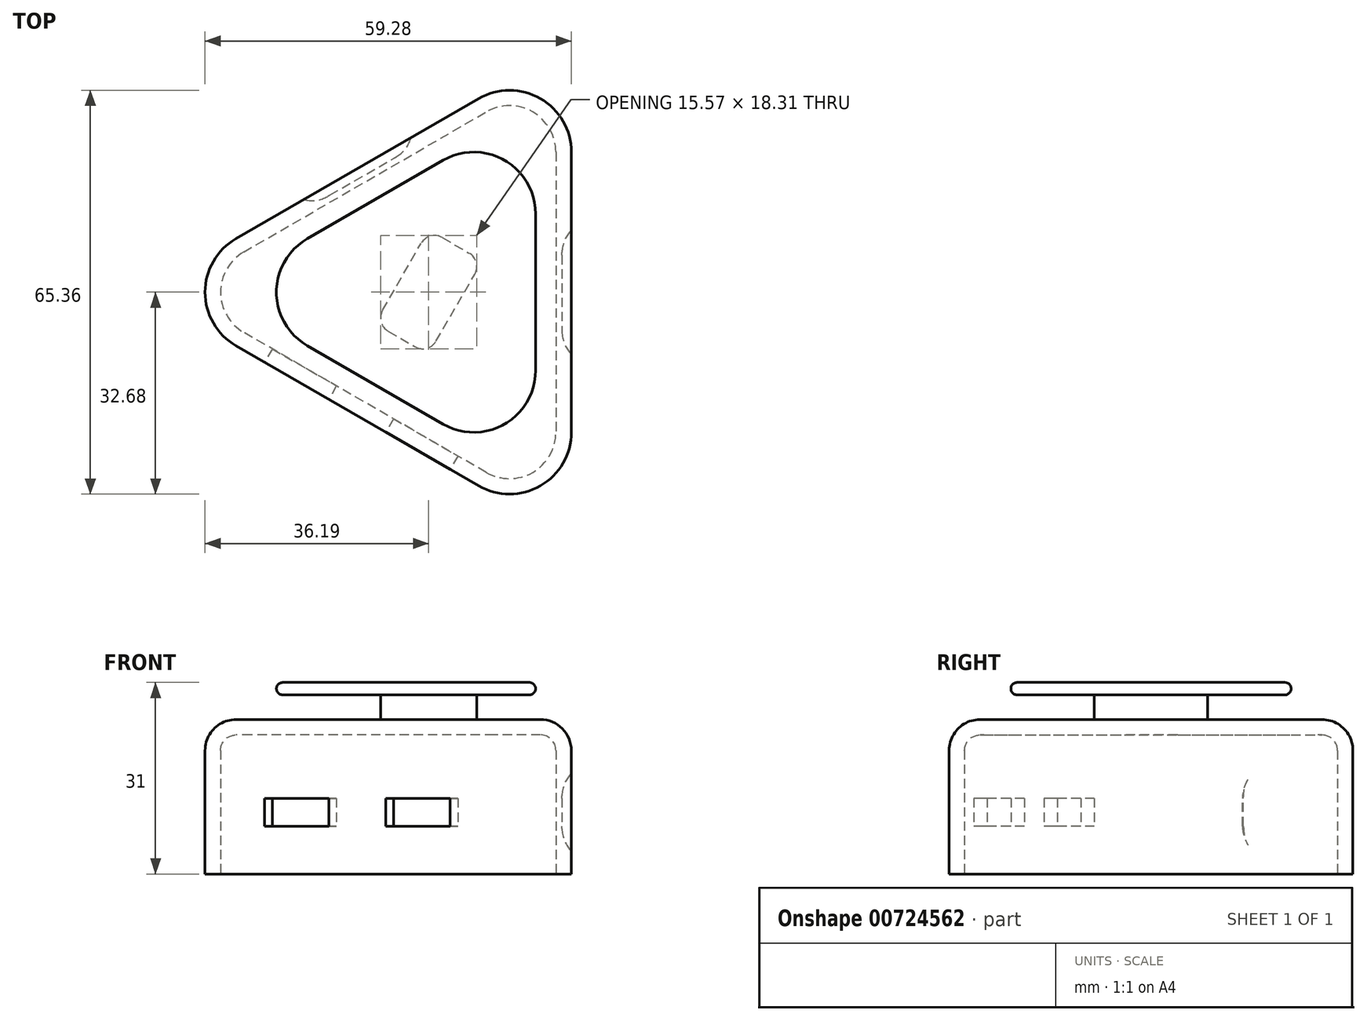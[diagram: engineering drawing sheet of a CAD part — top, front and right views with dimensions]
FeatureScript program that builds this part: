
annotation { "Feature Type Name" : "Feature", "Feature Type Description" : "" }
export const myFeature = defineFeature(function(context is Context, id is Id, definition is map)
    precondition{}
    {
        {
            var Q0;
            Q0=qCreatedBy(makeId("Top.planeOp"),FACE);
            var sketch = newSketch(context, id + "F0", { "sketchPlane" : qUnion([Q0])});
            skCircle(sketch, "E0.cCircle", {"center": v(0, 0) * mm, "radius": 23.1 * mm, "construction": true});
            skLineSegment(sketch, "E0.0", {"start": v(23.1, 40) * mm, "end": v(23.1, -40) * mm});
            skLineSegment(sketch, "E0.1", {"start": v(23.1, -40) * mm, "end": v(-46.19, 0) * mm});
            skLineSegment(sketch, "E0.2", {"start": v(-46.19, 0) * mm, "end": v(23.1, 40) * mm});
            skPoint(sketch, "E0.0.midPoint", {"position": v(23.1, 0) * mm});
            skSolve(sketch);
        }
        {
            var Q0;
            Q0=makeQuery(id+"F0.imprint","IMPRINT",FACE,{"disambiguationData":[TD([[makeQuery(id+"F0.imprint","IMPRINT",EDGE,{"derivedFrom":sQuery(id+"F0.wireOp",EDGE,"E0.0")}),-1.0]])]});
            extrude(context, id + "F1", {"entities" : qUnion([Q0]), "depth" : 25 * mm, "offsetDistance" : 25 * mm});
        }
        {
            var Q0;
            Q0=makeQuery(id+"F1.opExtrude","SWEPT_EDGE",EDGE,{"disambiguationData":[OSD([sQuery(id+"F0.wireOp",EDGE,"E0.1"),sQuery(id+"F0.wireOp",EDGE,"E0.2")])]});
            var Q1;
            Q1=makeQuery(id+"F1.opExtrude","SWEPT_EDGE",EDGE,{"disambiguationData":[OSD([sQuery(id+"F0.wireOp",EDGE,"E0.0"),sQuery(id+"F0.wireOp",EDGE,"E0.1")])]});
            var Q2;
            Q2=makeQuery(id+"F1.opExtrude","SWEPT_EDGE",EDGE,{"disambiguationData":[OSD([sQuery(id+"F0.wireOp",EDGE,"E0.0"),sQuery(id+"F0.wireOp",EDGE,"E0.2")])]});
            fillet(context, id + "F2", {"entities" : qUnion([Q0, Q1, Q2]), "radius" : 10 * mm, "tangentPropagation" : true, "allowEdgeOverflow" : false});
        }
        {
            var Q0;
            Q0=makeQuery(id+"F1.opExtrude","CAP_EDGE",EDGE,{"disambiguationData":[OSD([sQuery(id+"F0.wireOp",EDGE,"E0.1")])],"isStart":false});
            fillet(context, id + "F3", {"entities" : qUnion([Q0]), "radius" : 5 * mm, "tangentPropagation" : true, "allowEdgeOverflow" : false});
        }
        {
            var Q0;
            Q0=makeQuery(id+"F1.opExtrude","CAP_FACE",FACE,{"disambiguationData":[OSD([sQuery(id+"F0.wireOp",EDGE,"E0.0"),sQuery(id+"F0.wireOp",EDGE,"E0.1"),sQuery(id+"F0.wireOp",EDGE,"E0.2")])],"isStart":true});
            shell(context, id + "F4", {"entities" : qUnion([Q0]), "thickness" : 2.5 * mm});
        }
        {
            var Q0;
            Q0=makeQuery(id+"F1.opExtrude","CAP_FACE",FACE,{"disambiguationData":[OSD([sQuery(id+"F0.wireOp",EDGE,"E0.0"),sQuery(id+"F0.wireOp",EDGE,"E0.1"),sQuery(id+"F0.wireOp",EDGE,"E0.2")])],"isStart":false});
            var sketch = newSketch(context, id + "F5", { "sketchPlane" : qUnion([Q0])});
            skLineSegment(sketch, "E1.bottom", {"start": v(-8.7, -5.08) * mm, "end": v(0.04, 10.08) * mm});
            skLineSegment(sketch, "E1.top", {"start": v(-0.04, -10.08) * mm, "end": v(8.7, 5.08) * mm});
            skLineSegment(sketch, "E1.left", {"start": v(-8.7, -5.08) * mm, "end": v(-0.04, -10.08) * mm});
            skLineSegment(sketch, "E1.right", {"start": v(0.04, 10.08) * mm, "end": v(8.7, 5.08) * mm});
            skPoint(sketch, "E1.middle", {"position": v(0, 0) * mm});
            skSolve(sketch);
        }
        {
            var Q0;
            Q0=makeQuery(id+"F5.imprint","IMPRINT",FACE,{"disambiguationData":[TD([[makeQuery(id+"F5.imprint","IMPRINT",EDGE,{"derivedFrom":sQuery(id+"F5.wireOp",EDGE,"E1.bottom")}),-1.0]])]});
            extrude(context, id + "F6", {"entities" : qUnion([Q0]), "operationType" : NewBodyOperationType.ADD, "depth" : 4 * mm, "offsetDistance" : 25 * mm});
        }
        {
            var Q0;
            Q0=makeQuery(id+"F6.opExtrude","SWEPT_EDGE",EDGE,{"disambiguationData":[OSD([sQuery(id+"F5.wireOp",EDGE,"E1.top"),sQuery(id+"F5.wireOp",EDGE,"E1.right")])]});
            var Q1;
            Q1=makeQuery(id+"F6.opExtrude","SWEPT_EDGE",EDGE,{"disambiguationData":[OSD([sQuery(id+"F5.wireOp",EDGE,"E1.bottom"),sQuery(id+"F5.wireOp",EDGE,"E1.right")])]});
            var Q2;
            Q2=makeQuery(id+"F6.opExtrude","SWEPT_EDGE",EDGE,{"disambiguationData":[OSD([sQuery(id+"F5.wireOp",EDGE,"E1.top"),sQuery(id+"F5.wireOp",EDGE,"E1.left")])]});
            var Q3;
            Q3=makeQuery(id+"F6.opExtrude","SWEPT_EDGE",EDGE,{"disambiguationData":[OSD([sQuery(id+"F5.wireOp",EDGE,"E1.bottom"),sQuery(id+"F5.wireOp",EDGE,"E1.left")])]});
            fillet(context, id + "F7", {"entities" : qUnion([Q0, Q1, Q2, Q3]), "radius" : 2.5 * mm, "tangentPropagation" : true, "allowEdgeOverflow" : false});
        }
        {
            var Q0;
            Q0=makeQuery(id+"F6.opExtrude","CAP_FACE",FACE,{"disambiguationData":[OSD([sQuery(id+"F5.wireOp",EDGE,"E1.bottom"),sQuery(id+"F5.wireOp",EDGE,"E1.top"),sQuery(id+"F5.wireOp",EDGE,"E1.left"),sQuery(id+"F5.wireOp",EDGE,"E1.right")])],"isStart":false});
            var sketch = newSketch(context, id + "F8", { "sketchPlane" : qUnion([Q0])});
            skCircle(sketch, "E2.cCircle", {"center": v(0, 0) * mm, "radius": 17.32 * mm, "construction": true});
            skLineSegment(sketch, "E2.0", {"start": v(17.32, 30) * mm, "end": v(17.32, -30) * mm});
            skLineSegment(sketch, "E2.1", {"start": v(17.32, -30) * mm, "end": v(-34.64, 0) * mm});
            skLineSegment(sketch, "E2.2", {"start": v(-34.64, 0) * mm, "end": v(17.32, 30) * mm});
            skPoint(sketch, "E2.0.midPoint", {"position": v(17.32, 0) * mm});
            skSolve(sketch);
        }
        {
            var Q0;
            Q0=makeQuery(id+"F8.imprint","IMPRINT",FACE,{"disambiguationData":[TD([[makeQuery(id+"F8.imprint","IMPRINT",EDGE,{"derivedFrom":sQuery(id+"F8.wireOp",EDGE,"E2.0")}),-1.0]])]});
            var Q1;
            {var subQ3=sQuery(id+"F5.wireOp",EDGE,"E1.bottom");Q1=makeQuery(id+"F8.imprint","IMPRINT",FACE,{"disambiguationData":[TD([[makeQuery(id+"F8.imprint","IMPRINT",EDGE,{"derivedFrom":makeQuery(id+"F6.opExtrude","CAP_EDGE",EDGE,{"disambiguationData":[OSD([subQ3])],"isStart":false})}),-1.0]])]});}
            extrude(context, id + "F9", {"entities" : qUnion([Q0, Q1]), "operationType" : NewBodyOperationType.ADD, "depth" : 2 * mm, "offsetDistance" : 25 * mm});
        }
        {
            var Q0;
            Q0=makeQuery(id+"F9.opExtrude","SWEPT_EDGE",EDGE,{"disambiguationData":[OSD([sQuery(id+"F8.wireOp",EDGE,"E2.1"),sQuery(id+"F8.wireOp",EDGE,"E2.2")])]});
            var Q1;
            Q1=makeQuery(id+"F9.opExtrude","SWEPT_EDGE",EDGE,{"disambiguationData":[OSD([sQuery(id+"F8.wireOp",EDGE,"E2.0"),sQuery(id+"F8.wireOp",EDGE,"E2.2")])]});
            var Q2;
            Q2=makeQuery(id+"F9.opExtrude","SWEPT_EDGE",EDGE,{"disambiguationData":[OSD([sQuery(id+"F8.wireOp",EDGE,"E2.0"),sQuery(id+"F8.wireOp",EDGE,"E2.1")])]});
            fillet(context, id + "F10", {"entities" : qUnion([Q0, Q1, Q2]), "radius" : 10 * mm, "tangentPropagation" : true, "allowEdgeOverflow" : false});
        }
        {
            var Q0;
            Q0=makeQuery(id+"F9.opExtrude","CAP_EDGE",EDGE,{"disambiguationData":[OSD([sQuery(id+"F8.wireOp",EDGE,"E2.2")])],"isStart":false});
            fillet(context, id + "F11", {"entities" : qUnion([Q0]), "radius" : 1 * mm, "tangentPropagation" : true, "allowEdgeOverflow" : false});
        }
        {
            var Q0;
            Q0=makeQuery(id+"F9.opExtrude","CAP_EDGE",EDGE,{"disambiguationData":[OSD([sQuery(id+"F8.wireOp",EDGE,"E2.2")])],"isStart":true});
            fillet(context, id + "F12", {"entities" : qUnion([Q0]), "radius" : 1 * mm, "tangentPropagation" : true, "allowEdgeOverflow" : false});
        }
        {
            var Q0;
            Q0=makeQuery(id+"F1.opExtrude","SWEPT_FACE",FACE,{"disambiguationData":[OSD([sQuery(id+"F0.wireOp",EDGE,"E0.1")])]});
            var sketch = newSketch(context, id + "F13", { "sketchPlane" : qUnion([Q0])});
            skLineSegment(sketch, "E3.bottom", {"start": v(5.34, 12.25) * mm, "end": v(17.34, 12.25) * mm});
            skLineSegment(sketch, "E3.top", {"start": v(5.34, 7.75) * mm, "end": v(17.34, 7.75) * mm});
            skLineSegment(sketch, "E3.left", {"start": v(5.34, 12.25) * mm, "end": v(5.34, 7.75) * mm});
            skLineSegment(sketch, "E3.right", {"start": v(17.34, 12.25) * mm, "end": v(17.34, 7.75) * mm});
            skPoint(sketch, "E3.middle", {"position": v(11.34, 10) * mm});
            skLineSegment(sketch, "E4.bottom", {"start": v(-17.34, 12.25) * mm, "end": v(-5.34, 12.25) * mm});
            skLineSegment(sketch, "E4.top", {"start": v(-17.34, 7.75) * mm, "end": v(-5.34, 7.75) * mm});
            skLineSegment(sketch, "E4.left", {"start": v(-17.34, 12.25) * mm, "end": v(-17.34, 7.75) * mm});
            skLineSegment(sketch, "E4.right", {"start": v(-5.34, 12.25) * mm, "end": v(-5.34, 7.75) * mm});
            skPoint(sketch, "E4.middle", {"position": v(-11.34, 10) * mm});
            skSolve(sketch);
        }
        {
            var Q0;
            Q0=makeQuery(id+"F13.imprint","IMPRINT",FACE,{"disambiguationData":[TD([[makeQuery(id+"F13.imprint","IMPRINT",EDGE,{"derivedFrom":sQuery(id+"F13.wireOp",EDGE,"E3.bottom")}),-1.0]])]});
            var Q1;
            Q1=makeQuery(id+"F13.imprint","IMPRINT",FACE,{"disambiguationData":[TD([[makeQuery(id+"F13.imprint","IMPRINT",EDGE,{"derivedFrom":sQuery(id+"F13.wireOp",EDGE,"E4.bottom")}),-1.0]])]});
            extrude(context, id + "F14", {"entities" : qUnion([Q0, Q1]), "operationType" : NewBodyOperationType.REMOVE, "oppositeDirection" : true, "depth" : 2.5 * mm, "offsetDistance" : 25 * mm});
        }
        {
            var Q0;
            Q0=makeQuery(id+"F1.opExtrude","SWEPT_FACE",FACE,{"disambiguationData":[OSD([sQuery(id+"F0.wireOp",EDGE,"E0.0")])]});
            var sketch = newSketch(context, id + "F15", { "sketchPlane" : qUnion([Q0])});
            skLineSegment(sketch, "E5", {"start": v(0, 20) * mm, "end": v(0, 0) * mm, "construction": true});
            skLineSegment(sketch, "E6", {"start": v(22.68, 10) * mm, "end": v(-22.68, 10) * mm, "construction": true});
            skLineSegment(sketch, "E7.bottom", {"start": v(6, 16.25) * mm, "end": v(-6, 16.25) * mm});
            skLineSegment(sketch, "E7.top", {"start": v(6, 3.75) * mm, "end": v(-6, 3.75) * mm});
            skLineSegment(sketch, "E7.left", {"start": v(10, 12.25) * mm, "end": v(10, 7.75) * mm});
            skLineSegment(sketch, "E7.right", {"start": v(-10, 12.25) * mm, "end": v(-10, 7.75) * mm});
            skPoint(sketch, "E7.middle", {"position": v(0, 10) * mm});
            skPoint(sketch, "E8.visualSharp", {"position": v(-10, 16.25) * mm});
            skArc(sketch, "E8.filletArc", {"start": v(-6, 16.25) * mm, "mid": v(-8.83, 15.08) * mm, "end": v(-10, 12.25) * mm});
            skPoint(sketch, "E9.visualSharp", {"position": v(10, 16.25) * mm});
            skArc(sketch, "E9.filletArc", {"start": v(10, 12.25) * mm, "mid": v(8.83, 15.08) * mm, "end": v(6, 16.25) * mm});
            skPoint(sketch, "E10.visualSharp", {"position": v(10, 3.75) * mm});
            skArc(sketch, "E10.filletArc", {"start": v(6, 3.75) * mm, "mid": v(8.83, 4.92) * mm, "end": v(10, 7.75) * mm});
            skPoint(sketch, "E11.visualSharp", {"position": v(-10, 3.75) * mm});
            skArc(sketch, "E11.filletArc", {"start": v(-10, 7.75) * mm, "mid": v(-8.83, 4.92) * mm, "end": v(-6, 3.75) * mm});
            skSolve(sketch);
        }
        {
            var Q0;
            Q0=makeQuery(id+"F1.opExtrude","SWEPT_FACE",FACE,{"disambiguationData":[OSD([sQuery(id+"F0.wireOp",EDGE,"E0.2")])]});
            var sketch = newSketch(context, id + "F16", { "sketchPlane" : qUnion([Q0])});
            skLineSegment(sketch, "E12", {"start": v(0, 0) * mm, "end": v(0, 20) * mm, "construction": true});
            skLineSegment(sketch, "E13.bottom", {"start": v(6, 16.25) * mm, "end": v(-6, 16.25) * mm});
            skLineSegment(sketch, "E13.top", {"start": v(6, 3.75) * mm, "end": v(-6, 3.75) * mm});
            skLineSegment(sketch, "E13.left", {"start": v(10, 12.25) * mm, "end": v(10, 7.75) * mm});
            skLineSegment(sketch, "E13.right", {"start": v(-10, 12.25) * mm, "end": v(-10, 7.75) * mm});
            skPoint(sketch, "E13.middle", {"position": v(0, 10) * mm});
            skPoint(sketch, "E14.visualSharp", {"position": v(-10, 16.25) * mm});
            skArc(sketch, "E14.filletArc", {"start": v(-6, 16.25) * mm, "mid": v(-8.83, 15.08) * mm, "end": v(-10, 12.25) * mm});
            skPoint(sketch, "E15.visualSharp", {"position": v(-10, 3.75) * mm});
            skArc(sketch, "E15.filletArc", {"start": v(-10, 7.75) * mm, "mid": v(-8.83, 4.92) * mm, "end": v(-6, 3.75) * mm});
            skPoint(sketch, "E16.visualSharp", {"position": v(10, 16.25) * mm});
            skArc(sketch, "E16.filletArc", {"start": v(10, 12.25) * mm, "mid": v(8.83, 15.08) * mm, "end": v(6, 16.25) * mm});
            skPoint(sketch, "E17.visualSharp", {"position": v(10, 3.75) * mm});
            skArc(sketch, "E17.filletArc", {"start": v(6, 3.75) * mm, "mid": v(8.83, 4.92) * mm, "end": v(10, 7.75) * mm});
            skSolve(sketch);
        }
        {
            var Q0;
            Q0=makeQuery(id+"F15.imprint","IMPRINT",FACE,{"disambiguationData":[TD([[makeQuery(id+"F15.imprint","IMPRINT",EDGE,{"derivedFrom":sQuery(id+"F15.wireOp",EDGE,"E7.bottom")}),1.0]])]});
            extrude(context, id + "F17", {"entities" : qUnion([Q0]), "operationType" : NewBodyOperationType.REMOVE, "oppositeDirection" : true, "depth" : 1.5 * mm, "offsetDistance" : 25 * mm});
        }
        {
            var Q0;
            Q0=makeQuery(id+"F16.imprint","IMPRINT",FACE,{"disambiguationData":[TD([[makeQuery(id+"F16.imprint","IMPRINT",EDGE,{"derivedFrom":sQuery(id+"F16.wireOp",EDGE,"E13.bottom")}),1.0]])]});
            extrude(context, id + "F18", {"entities" : qUnion([Q0]), "operationType" : NewBodyOperationType.REMOVE, "oppositeDirection" : true, "depth" : 1.5 * mm, "offsetDistance" : 25 * mm});
        }
        {
            var Q0;
            Q0=makeQuery(id+"F17.boolean.opBoolean","COPY",EDGE,{"derivedFrom":makeQuery(id+"F17.opExtrude","CAP_EDGE",EDGE,{"disambiguationData":[OSD([sQuery(id+"F15.wireOp",EDGE,"E7.right")])],"isStart":false})});
            var Q1;
            Q1=makeQuery(id+"F17.boolean.opBoolean","COPY",EDGE,{"derivedFrom":makeQuery(id+"F17.opExtrude","CAP_EDGE",EDGE,{"disambiguationData":[OSD([sQuery(id+"F15.wireOp",EDGE,"E8.filletArc")])],"isStart":false})});
            var Q2;
            Q2=makeQuery(id+"F17.boolean.opBoolean","COPY",EDGE,{"derivedFrom":makeQuery(id+"F17.opExtrude","CAP_EDGE",EDGE,{"disambiguationData":[OSD([sQuery(id+"F15.wireOp",EDGE,"E7.bottom")])],"isStart":false})});
            var Q3;
            Q3=makeQuery(id+"F17.boolean.opBoolean","COPY",EDGE,{"derivedFrom":makeQuery(id+"F17.opExtrude","CAP_EDGE",EDGE,{"disambiguationData":[OSD([sQuery(id+"F15.wireOp",EDGE,"E9.filletArc")])],"isStart":false})});
            var Q4;
            Q4=makeQuery(id+"F17.boolean.opBoolean","COPY",EDGE,{"derivedFrom":makeQuery(id+"F17.opExtrude","CAP_EDGE",EDGE,{"disambiguationData":[OSD([sQuery(id+"F15.wireOp",EDGE,"E7.left")])],"isStart":false})});
            var Q5;
            Q5=makeQuery(id+"F17.boolean.opBoolean","COPY",EDGE,{"derivedFrom":makeQuery(id+"F17.opExtrude","CAP_EDGE",EDGE,{"disambiguationData":[OSD([sQuery(id+"F15.wireOp",EDGE,"E10.filletArc")])],"isStart":false})});
            var Q6;
            Q6=makeQuery(id+"F17.boolean.opBoolean","COPY",EDGE,{"derivedFrom":makeQuery(id+"F17.opExtrude","CAP_EDGE",EDGE,{"disambiguationData":[OSD([sQuery(id+"F15.wireOp",EDGE,"E7.top")])],"isStart":false})});
            var Q7;
            Q7=makeQuery(id+"F17.boolean.opBoolean","COPY",EDGE,{"derivedFrom":makeQuery(id+"F17.opExtrude","CAP_EDGE",EDGE,{"disambiguationData":[OSD([sQuery(id+"F15.wireOp",EDGE,"E11.filletArc")])],"isStart":false})});
            var Q8;
            Q8=makeQuery(id+"F18.boolean.opBoolean","COPY",EDGE,{"derivedFrom":makeQuery(id+"F18.opExtrude","CAP_EDGE",EDGE,{"disambiguationData":[OSD([sQuery(id+"F16.wireOp",EDGE,"E13.right")])],"isStart":false})});
            var Q9;
            Q9=makeQuery(id+"F18.boolean.opBoolean","COPY",EDGE,{"derivedFrom":makeQuery(id+"F18.opExtrude","CAP_EDGE",EDGE,{"disambiguationData":[OSD([sQuery(id+"F16.wireOp",EDGE,"E14.filletArc")])],"isStart":false})});
            var Q10;
            Q10=makeQuery(id+"F18.boolean.opBoolean","COPY",EDGE,{"derivedFrom":makeQuery(id+"F18.opExtrude","CAP_EDGE",EDGE,{"disambiguationData":[OSD([sQuery(id+"F16.wireOp",EDGE,"E13.bottom")])],"isStart":false})});
            var Q11;
            Q11=makeQuery(id+"F18.boolean.opBoolean","COPY",EDGE,{"derivedFrom":makeQuery(id+"F18.opExtrude","CAP_EDGE",EDGE,{"disambiguationData":[OSD([sQuery(id+"F16.wireOp",EDGE,"E17.filletArc")])],"isStart":false})});
            var Q12;
            Q12=makeQuery(id+"F18.boolean.opBoolean","COPY",EDGE,{"derivedFrom":makeQuery(id+"F18.opExtrude","CAP_EDGE",EDGE,{"disambiguationData":[OSD([sQuery(id+"F16.wireOp",EDGE,"E16.filletArc")])],"isStart":false})});
            var Q13;
            Q13=makeQuery(id+"F18.boolean.opBoolean","COPY",EDGE,{"derivedFrom":makeQuery(id+"F18.opExtrude","CAP_EDGE",EDGE,{"disambiguationData":[OSD([sQuery(id+"F16.wireOp",EDGE,"E13.left")])],"isStart":false})});
            var Q14;
            Q14=makeQuery(id+"F18.boolean.opBoolean","COPY",EDGE,{"derivedFrom":makeQuery(id+"F18.opExtrude","CAP_EDGE",EDGE,{"disambiguationData":[OSD([sQuery(id+"F16.wireOp",EDGE,"E13.top")])],"isStart":false})});
            var Q15;
            Q15=makeQuery(id+"F18.boolean.opBoolean","COPY",EDGE,{"derivedFrom":makeQuery(id+"F18.opExtrude","CAP_EDGE",EDGE,{"disambiguationData":[OSD([sQuery(id+"F16.wireOp",EDGE,"E15.filletArc")])],"isStart":false})});
            fillet(context, id + "F19", {"entities" : qUnion([Q0, Q1, Q2, Q3, Q4, Q5, Q6, Q7, Q8, Q9, Q10, Q11, Q12, Q13, Q14, Q15]), "radius" : 5 * mm, "tangentPropagation" : true, "allowEdgeOverflow" : false});
        }
        {
            var Q0;
            Q0=makeQuery(id+"F19.opFillet","BLEND_EDGE",EDGE,{"disambiguationData":[OD(1.0)],"blendedFrom":[makeQuery(id+"F17.boolean.opBoolean","COPY",EDGE,{"derivedFrom":makeQuery(id+"F17.opExtrude","CAP_EDGE",EDGE,{"disambiguationData":[OSD([sQuery(id+"F15.wireOp",EDGE,"E7.right")])],"isStart":false})}),makeQuery(id+"F1.opExtrude","SWEPT_FACE",FACE,{"disambiguationData":[OSD([sQuery(id+"F0.wireOp",EDGE,"E0.0")])]})],"blendedInto":[makeQuery(id+"F1.opExtrude","SWEPT_FACE",FACE,{"disambiguationData":[OSD([sQuery(id+"F0.wireOp",EDGE,"E0.0")])]})]});
            var Q1;
            Q1=makeQuery(id+"F19.opFillet","BLEND_EDGE",EDGE,{"disambiguationData":[OD(0.0)],"blendedFrom":[makeQuery(id+"F17.boolean.opBoolean","COPY",EDGE,{"derivedFrom":makeQuery(id+"F17.opExtrude","CAP_EDGE",EDGE,{"disambiguationData":[OSD([sQuery(id+"F15.wireOp",EDGE,"E7.right")])],"isStart":false})}),makeQuery(id+"F1.opExtrude","SWEPT_FACE",FACE,{"disambiguationData":[OSD([sQuery(id+"F0.wireOp",EDGE,"E0.0")])]})],"blendedInto":[makeQuery(id+"F1.opExtrude","SWEPT_FACE",FACE,{"disambiguationData":[OSD([sQuery(id+"F0.wireOp",EDGE,"E0.0")])]})]});
            var Q2;
            Q2=makeQuery(id+"F19.opFillet","BLEND_EDGE",EDGE,{"disambiguationData":[OD(1.0)],"blendedFrom":[makeQuery(id+"F17.boolean.opBoolean","COPY",EDGE,{"derivedFrom":makeQuery(id+"F17.opExtrude","CAP_EDGE",EDGE,{"disambiguationData":[OSD([sQuery(id+"F15.wireOp",EDGE,"E7.bottom")])],"isStart":false})}),makeQuery(id+"F1.opExtrude","SWEPT_FACE",FACE,{"disambiguationData":[OSD([sQuery(id+"F0.wireOp",EDGE,"E0.0")])]})],"blendedInto":[makeQuery(id+"F1.opExtrude","SWEPT_FACE",FACE,{"disambiguationData":[OSD([sQuery(id+"F0.wireOp",EDGE,"E0.0")])]})]});
            var Q3;
            Q3=makeQuery(id+"F19.opFillet","BLEND_EDGE",EDGE,{"disambiguationData":[OD(0.0)],"blendedFrom":[makeQuery(id+"F17.boolean.opBoolean","COPY",EDGE,{"derivedFrom":makeQuery(id+"F17.opExtrude","CAP_EDGE",EDGE,{"disambiguationData":[OSD([sQuery(id+"F15.wireOp",EDGE,"E7.bottom")])],"isStart":false})}),makeQuery(id+"F1.opExtrude","SWEPT_FACE",FACE,{"disambiguationData":[OSD([sQuery(id+"F0.wireOp",EDGE,"E0.0")])]})],"blendedInto":[makeQuery(id+"F1.opExtrude","SWEPT_FACE",FACE,{"disambiguationData":[OSD([sQuery(id+"F0.wireOp",EDGE,"E0.0")])]})]});
            var Q4;
            Q4=makeQuery(id+"F19.opFillet","BLEND_EDGE",EDGE,{"disambiguationData":[OD(0.0)],"blendedFrom":[makeQuery(id+"F17.boolean.opBoolean","COPY",EDGE,{"derivedFrom":makeQuery(id+"F17.opExtrude","CAP_EDGE",EDGE,{"disambiguationData":[OSD([sQuery(id+"F15.wireOp",EDGE,"E7.left")])],"isStart":false})}),makeQuery(id+"F1.opExtrude","SWEPT_FACE",FACE,{"disambiguationData":[OSD([sQuery(id+"F0.wireOp",EDGE,"E0.0")])]})],"blendedInto":[makeQuery(id+"F1.opExtrude","SWEPT_FACE",FACE,{"disambiguationData":[OSD([sQuery(id+"F0.wireOp",EDGE,"E0.0")])]})]});
            var Q5;
            Q5=makeQuery(id+"F19.opFillet","BLEND_EDGE",EDGE,{"disambiguationData":[OD(1.0)],"blendedFrom":[makeQuery(id+"F17.boolean.opBoolean","COPY",EDGE,{"derivedFrom":makeQuery(id+"F17.opExtrude","CAP_EDGE",EDGE,{"disambiguationData":[OSD([sQuery(id+"F15.wireOp",EDGE,"E7.left")])],"isStart":false})}),makeQuery(id+"F1.opExtrude","SWEPT_FACE",FACE,{"disambiguationData":[OSD([sQuery(id+"F0.wireOp",EDGE,"E0.0")])]})],"blendedInto":[makeQuery(id+"F1.opExtrude","SWEPT_FACE",FACE,{"disambiguationData":[OSD([sQuery(id+"F0.wireOp",EDGE,"E0.0")])]})]});
            var Q6;
            Q6=makeQuery(id+"F19.opFillet","BLEND_EDGE",EDGE,{"disambiguationData":[OD(0.0)],"blendedFrom":[makeQuery(id+"F17.boolean.opBoolean","COPY",EDGE,{"derivedFrom":makeQuery(id+"F17.opExtrude","CAP_EDGE",EDGE,{"disambiguationData":[OSD([sQuery(id+"F15.wireOp",EDGE,"E7.top")])],"isStart":false})}),makeQuery(id+"F1.opExtrude","SWEPT_FACE",FACE,{"disambiguationData":[OSD([sQuery(id+"F0.wireOp",EDGE,"E0.0")])]})],"blendedInto":[makeQuery(id+"F1.opExtrude","SWEPT_FACE",FACE,{"disambiguationData":[OSD([sQuery(id+"F0.wireOp",EDGE,"E0.0")])]})]});
            var Q7;
            Q7=makeQuery(id+"F19.opFillet","BLEND_EDGE",EDGE,{"disambiguationData":[OD(1.0)],"blendedFrom":[makeQuery(id+"F17.boolean.opBoolean","COPY",EDGE,{"derivedFrom":makeQuery(id+"F17.opExtrude","CAP_EDGE",EDGE,{"disambiguationData":[OSD([sQuery(id+"F15.wireOp",EDGE,"E7.top")])],"isStart":false})}),makeQuery(id+"F1.opExtrude","SWEPT_FACE",FACE,{"disambiguationData":[OSD([sQuery(id+"F0.wireOp",EDGE,"E0.0")])]})],"blendedInto":[makeQuery(id+"F1.opExtrude","SWEPT_FACE",FACE,{"disambiguationData":[OSD([sQuery(id+"F0.wireOp",EDGE,"E0.0")])]})]});
            var Q8;
            Q8=makeQuery(id+"F19.opFillet","BLEND_EDGE",EDGE,{"disambiguationData":[OD(0.0)],"blendedFrom":[makeQuery(id+"F18.boolean.opBoolean","COPY",EDGE,{"derivedFrom":makeQuery(id+"F18.opExtrude","CAP_EDGE",EDGE,{"disambiguationData":[OSD([sQuery(id+"F16.wireOp",EDGE,"E13.left")])],"isStart":false})}),makeQuery(id+"F1.opExtrude","SWEPT_FACE",FACE,{"disambiguationData":[OSD([sQuery(id+"F0.wireOp",EDGE,"E0.2")])]})],"blendedInto":[makeQuery(id+"F1.opExtrude","SWEPT_FACE",FACE,{"disambiguationData":[OSD([sQuery(id+"F0.wireOp",EDGE,"E0.2")])]})]});
            var Q9;
            Q9=makeQuery(id+"F19.opFillet","BLEND_EDGE",EDGE,{"disambiguationData":[OD(0.0)],"blendedFrom":[makeQuery(id+"F18.boolean.opBoolean","COPY",EDGE,{"derivedFrom":makeQuery(id+"F18.opExtrude","CAP_EDGE",EDGE,{"disambiguationData":[OSD([sQuery(id+"F16.wireOp",EDGE,"E13.bottom")])],"isStart":false})}),makeQuery(id+"F1.opExtrude","SWEPT_FACE",FACE,{"disambiguationData":[OSD([sQuery(id+"F0.wireOp",EDGE,"E0.2")])]})],"blendedInto":[makeQuery(id+"F1.opExtrude","SWEPT_FACE",FACE,{"disambiguationData":[OSD([sQuery(id+"F0.wireOp",EDGE,"E0.2")])]})]});
            var Q10;
            Q10=makeQuery(id+"F19.opFillet","BLEND_EDGE",EDGE,{"disambiguationData":[OD(1.0)],"blendedFrom":[makeQuery(id+"F18.boolean.opBoolean","COPY",EDGE,{"derivedFrom":makeQuery(id+"F18.opExtrude","CAP_EDGE",EDGE,{"disambiguationData":[OSD([sQuery(id+"F16.wireOp",EDGE,"E13.bottom")])],"isStart":false})}),makeQuery(id+"F1.opExtrude","SWEPT_FACE",FACE,{"disambiguationData":[OSD([sQuery(id+"F0.wireOp",EDGE,"E0.2")])]})],"blendedInto":[makeQuery(id+"F1.opExtrude","SWEPT_FACE",FACE,{"disambiguationData":[OSD([sQuery(id+"F0.wireOp",EDGE,"E0.2")])]})]});
            var Q11;
            Q11=makeQuery(id+"F19.opFillet","BLEND_EDGE",EDGE,{"disambiguationData":[OD(0.0)],"blendedFrom":[makeQuery(id+"F18.boolean.opBoolean","COPY",EDGE,{"derivedFrom":makeQuery(id+"F18.opExtrude","CAP_EDGE",EDGE,{"disambiguationData":[OSD([sQuery(id+"F16.wireOp",EDGE,"E13.right")])],"isStart":false})}),makeQuery(id+"F1.opExtrude","SWEPT_FACE",FACE,{"disambiguationData":[OSD([sQuery(id+"F0.wireOp",EDGE,"E0.2")])]})],"blendedInto":[makeQuery(id+"F1.opExtrude","SWEPT_FACE",FACE,{"disambiguationData":[OSD([sQuery(id+"F0.wireOp",EDGE,"E0.2")])]})]});
            var Q12;
            Q12=makeQuery(id+"F19.opFillet","BLEND_EDGE",EDGE,{"disambiguationData":[OD(1.0)],"blendedFrom":[makeQuery(id+"F18.boolean.opBoolean","COPY",EDGE,{"derivedFrom":makeQuery(id+"F18.opExtrude","CAP_EDGE",EDGE,{"disambiguationData":[OSD([sQuery(id+"F16.wireOp",EDGE,"E13.left")])],"isStart":false})}),makeQuery(id+"F1.opExtrude","SWEPT_FACE",FACE,{"disambiguationData":[OSD([sQuery(id+"F0.wireOp",EDGE,"E0.2")])]})],"blendedInto":[makeQuery(id+"F1.opExtrude","SWEPT_FACE",FACE,{"disambiguationData":[OSD([sQuery(id+"F0.wireOp",EDGE,"E0.2")])]})]});
            var Q13;
            Q13=makeQuery(id+"F19.opFillet","BLEND_EDGE",EDGE,{"disambiguationData":[OD(1.0)],"blendedFrom":[makeQuery(id+"F18.boolean.opBoolean","COPY",EDGE,{"derivedFrom":makeQuery(id+"F18.opExtrude","CAP_EDGE",EDGE,{"disambiguationData":[OSD([sQuery(id+"F16.wireOp",EDGE,"E13.right")])],"isStart":false})}),makeQuery(id+"F1.opExtrude","SWEPT_FACE",FACE,{"disambiguationData":[OSD([sQuery(id+"F0.wireOp",EDGE,"E0.2")])]})],"blendedInto":[makeQuery(id+"F1.opExtrude","SWEPT_FACE",FACE,{"disambiguationData":[OSD([sQuery(id+"F0.wireOp",EDGE,"E0.2")])]})]});
            var Q14;
            Q14=makeQuery(id+"F19.opFillet","BLEND_EDGE",EDGE,{"disambiguationData":[OD(1.0)],"blendedFrom":[makeQuery(id+"F18.boolean.opBoolean","COPY",EDGE,{"derivedFrom":makeQuery(id+"F18.opExtrude","CAP_EDGE",EDGE,{"disambiguationData":[OSD([sQuery(id+"F16.wireOp",EDGE,"E13.top")])],"isStart":false})}),makeQuery(id+"F1.opExtrude","SWEPT_FACE",FACE,{"disambiguationData":[OSD([sQuery(id+"F0.wireOp",EDGE,"E0.2")])]})],"blendedInto":[makeQuery(id+"F1.opExtrude","SWEPT_FACE",FACE,{"disambiguationData":[OSD([sQuery(id+"F0.wireOp",EDGE,"E0.2")])]})]});
            var Q15;
            Q15=makeQuery(id+"F19.opFillet","BLEND_EDGE",EDGE,{"disambiguationData":[OD(0.0)],"blendedFrom":[makeQuery(id+"F18.boolean.opBoolean","COPY",EDGE,{"derivedFrom":makeQuery(id+"F18.opExtrude","CAP_EDGE",EDGE,{"disambiguationData":[OSD([sQuery(id+"F16.wireOp",EDGE,"E13.top")])],"isStart":false})}),makeQuery(id+"F1.opExtrude","SWEPT_FACE",FACE,{"disambiguationData":[OSD([sQuery(id+"F0.wireOp",EDGE,"E0.2")])]})],"blendedInto":[makeQuery(id+"F1.opExtrude","SWEPT_FACE",FACE,{"disambiguationData":[OSD([sQuery(id+"F0.wireOp",EDGE,"E0.2")])]})]});
            fillet(context, id + "F20", {"entities" : qUnion([Q0, Q1, Q2, Q3, Q4, Q5, Q6, Q7, Q8, Q9, Q10, Q11, Q12, Q13, Q14, Q15]), "radius" : 0.5 * mm, "tangentPropagation" : true, "allowEdgeOverflow" : false});
        }
    });
